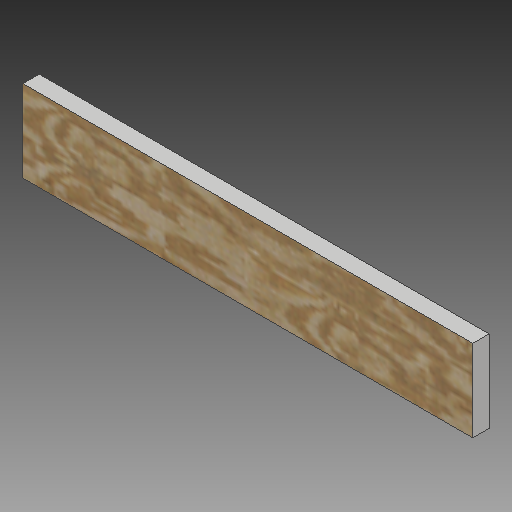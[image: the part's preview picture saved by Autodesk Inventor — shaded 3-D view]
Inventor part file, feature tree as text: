
AUTODESK INVENTOR PART (.ipt)
format: ipt  version: 2018.2 (Build 222227000, 227)  size: 179,200 bytes
history: native  units: in
note: dims shown in document units (in); Inventor stores cm internally (conversion verified against a paired STEP export)
features: other x4, reference x2, extrude x1, sketch x1
ambient origin geometry x8: Origin, YZ Plane, XZ Plane, XY Plane, X Axis, Y Axis, Z Axis, Center Point
bodies: Solid1 (feature_tree)
feature tree (8):
  extrude  "Extrusion1"  Depth=5.0in
  sketch  "Sketch1"  dims[d0=1.0in d1=0.0in d2=28.226in d4=5.0in]
  reference  "Reference1"
  reference  "Reference2"
  parser-record x1  (decoder bookkeeping rows leaked as tree rows — omitted from the tree; the rows remain in map.json)
  other  "Mounting Part figureing outness.iam"
  other  "Plywood Base - Bottom:1"
  other  "2835T310_MIGHTY-LITE CASTER:6"
note: 1 file-system path scrubbed to <path> (originals preserved in map.json)
